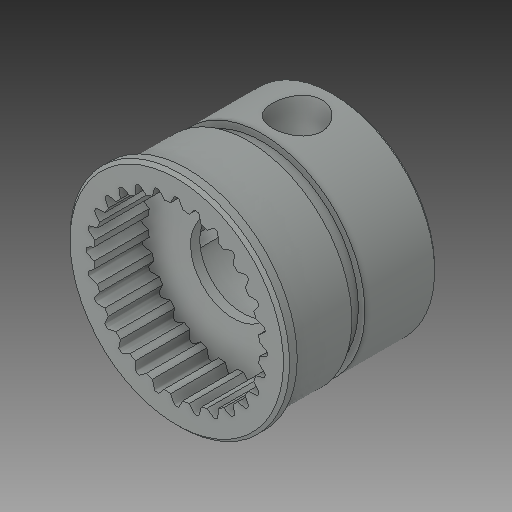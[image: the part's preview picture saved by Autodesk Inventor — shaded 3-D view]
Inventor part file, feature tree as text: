
AUTODESK INVENTOR PART (.ipt)
format: ipt  version: 2017 (Build 210142000, 142)  size: 396,288 bytes
history: native  units: in
note: dims shown in document units (in); Inventor stores cm internally (conversion verified against a paired STEP export)
features: fillet x1
ambient origin geometry x8: Origin, YZ Plane, XZ Plane, XY Plane, X Axis, Y Axis, Z Axis, Center Point
bodies: Solid1 (feature_tree)
feature tree (1):
  fillet  "Fillet1"  [1 undecoded]
note: 1 required parameter value undecoded (feature->parameter linkage not recoverable at this tier; creation-order binding heuristic only, values carry confidence <= 0.55)
